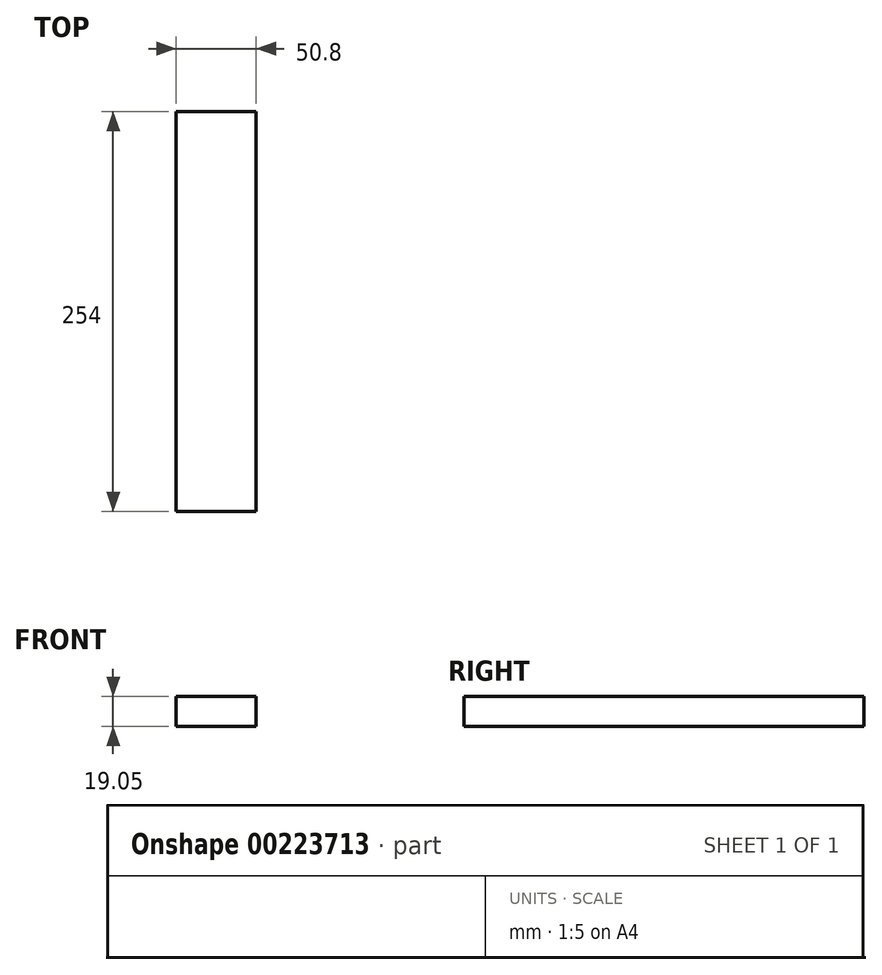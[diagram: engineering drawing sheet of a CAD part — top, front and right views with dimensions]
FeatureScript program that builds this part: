
annotation { "Feature Type Name" : "Feature", "Feature Type Description" : "" }
export const myFeature = defineFeature(function(context is Context, id is Id, definition is map)
    precondition{}
    {
        {
            var Q0;
            Q0=qCreatedBy(makeId("Top.planeOp"),FACE);
            var sketch = newSketch(context, id + "F0", { "sketchPlane" : qUnion([Q0])});
            skLineSegment(sketch, "E0.bottom", {"start": v(0, 0) * mm, "end": v(50.8, 0) * mm});
            skLineSegment(sketch, "E0.top", {"start": v(0, -254) * mm, "end": v(50.8, -254) * mm});
            skLineSegment(sketch, "E0.left", {"start": v(0, 0) * mm, "end": v(0, -254) * mm});
            skLineSegment(sketch, "E0.right", {"start": v(50.8, 0) * mm, "end": v(50.8, -254) * mm});
            skSolve(sketch);
        }
        {
            var Q0;
            Q0=makeQuery(id+"F0.imprint","IMPRINT",FACE,{"disambiguationData":[TD([[makeQuery(id+"F0.imprint","IMPRINT",EDGE,{"derivedFrom":sQuery(id+"F0.wireOp",EDGE,"E0.bottom")}),-1.0]])]});
            extrude(context, id + "F1", {"entities" : qUnion([Q0]), "depth" : 19.05 * mm});
        }
    });
